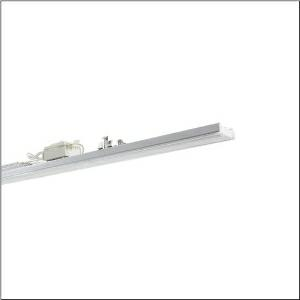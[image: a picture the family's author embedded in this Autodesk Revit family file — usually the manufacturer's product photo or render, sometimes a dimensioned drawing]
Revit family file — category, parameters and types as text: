
# Revit family: licross_21_recessed_mo_52tl12dn47xg
name_source: partatom
category: Lighting Fixtures
units: mm (PartAtom-declared; Revit-internal decimal feet)

## family parameters
Cut with Voids When Loaded = No
Host = Face
Light Source = No
Part Type = Normal
Room Calculation Point = No
Round Connector Dimension = Use Diameter
Shared = No

## types (1)
- --- (1 x LED, 7230 lm, 39.3 W, 4000K)
    Apparent Load = 39 VA
    CIE Flux Codes = 72 92 99 100 100
    Color Rendering = 80
    Color Temperature = 4000K
    Default Elevation = 1800 mm
    Description = Licross 21 Recessed MO, luminaire insert, of sheet steel, galvanised, coil coated, white, length: 1.500mm, width: 66mm, height: 67mm, LED rated luminous flux: 7.230lm, light colour: 840, SDCM (Standard Deviation of Colour Matching)MacAdam ≤ 3 SDCM (initial), control gear: DALI 2, with plug, 5-pole, with phase selection, mains connection: 220..240V, AC, 50/60Hz, rated input power: 39W, internal wiring halogen-free, primary optical cover: cover, of PMMA, light emission: direct distribution, primary light characteristic: symmetric, protection rating (complete): IP40, insulation class (complete): insulation class I (protective earthing), certification: CE, ENEC, VDE, UKCA, protection symbol: D if used in an environment without relevant dust loads with corresponding accessories, impact resistance: IK06, permissible ambient temperature for indoor applications: -25..+40°C, corresponds to IFS (International Featured Standards) requirements for safety and quality in the food industry, reducing of maximum allowable ambient temperature of 5°C with ceiling mounting, LABS conformity tested according to VDMA 24364:2018-05, The light source and the operating device comply with the requirements of the Ecodesign Regulation (EU) 2019/2020 and are replaceable in accordance with this regulation, packaging unit: 1 piece
    Height = 58 mm
    Lamp = 1 x LED
    Lamp Light Flux = 7230 lm
    Lamp Power = 39.3 W
    Lamp count = 1
    Length = 1500 mm
    Luminous efficacy = 184 lm/W
    Manufacturer = Siteco
    ModVariant = No
    Model = 52TL12DN47XG
    Mounting Place = Ceiling
    Mounting Type = Pendant
    Number of Poles = 1
    OnlyDefault = Yes
    Power Factor = 1
    Product Name = Licross 21 Recessed MO
    Product group = luminaire insert | ceiling pendant
    ProductGroupID = 901
    Protection Class = Protection class I
    Protection Degree = IP 40
    RLX_Detail_Level = 1
    RLX_Emergency_Light_Flux = 0 lm
    RLX_Emergency_Type = 0
    RLX_Emergency_Type_DB = No
    RlxData = <blob elided: 24453 chars, md5=47c345df>
    Socket = socket
    Standby Power = 0 W
    System Light Flux = 7230 lm
    System Power = 39 W
    Type Comments = factory setting: luminous flux: 100 % | dim-lin: 254 | 267 mA
    Type Image = l_1296930.jpg
    URL = http://relux.com
    VarID = @adj_126457
    Voltage = 0 V
    Weight = 0.00 kg
    Width = 66 mm

## geometry (parser evidence)
native form markers: Blend x4, Sweep x10
no freeform markers — native parametric forms only
